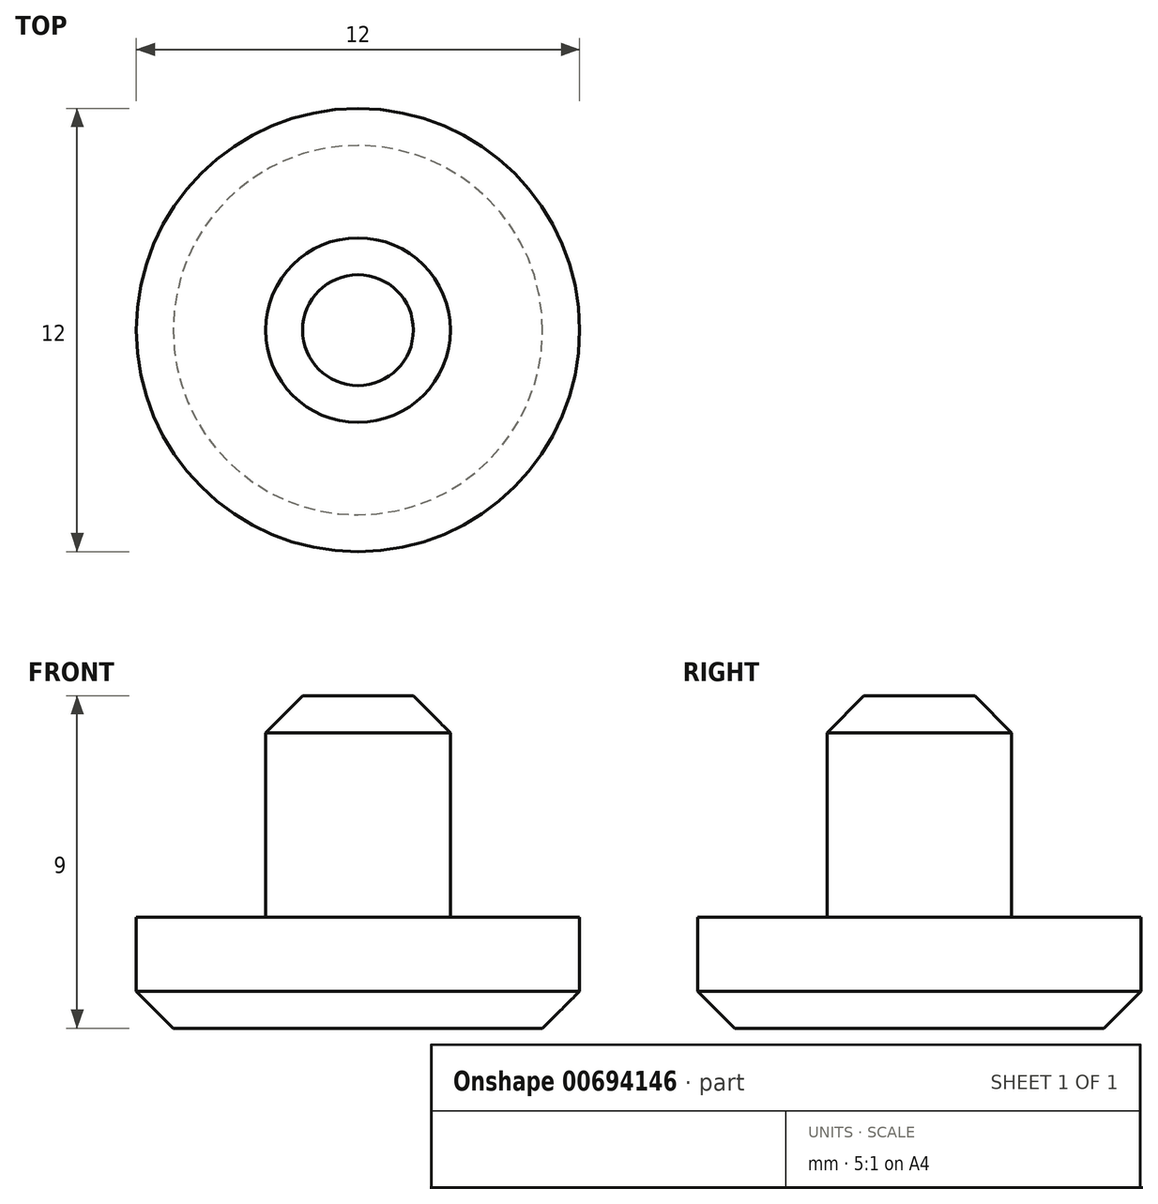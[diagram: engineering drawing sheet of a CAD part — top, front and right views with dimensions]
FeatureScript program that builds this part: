
annotation { "Feature Type Name" : "Feature", "Feature Type Description" : "" }
export const myFeature = defineFeature(function(context is Context, id is Id, definition is map)
    precondition{}
    {
        {
            var Q0;
            Q0=qCreatedBy(makeId("Top.planeOp"),FACE);
            var sketch = newSketch(context, id + "F0", { "sketchPlane" : qUnion([Q0])});
            skCircle(sketch, "E0", {"center": v(0, 0) * mm, "radius": 6 * mm});
            skCircle(sketch, "E1", {"center": v(0, 0) * mm, "radius": 2.5 * mm});
            skSolve(sketch);
        }
        {
            var Q0;
            Q0=makeQuery(id+"F0.imprint","IMPRINT",FACE,{"disambiguationData":[TD([[makeQuery(id+"F0.imprint","IMPRINT",EDGE,{"derivedFrom":sQuery(id+"F0.wireOp",EDGE,"E0")}),1.0]])]});
            var Q1;
            Q1=makeQuery(id+"F0.imprint","IMPRINT",FACE,{"disambiguationData":[TD([[makeQuery(id+"F0.imprint","IMPRINT",EDGE,{"derivedFrom":sQuery(id+"F0.wireOp",EDGE,"E1")}),1.0]])]});
            extrude(context, id + "F1", {"entities" : qUnion([Q0, Q1]), "oppositeDirection" : true, "depth" : 3 * mm, "offsetDistance" : 25 * mm});
        }
        {
            var Q0;
            Q0=makeQuery(id+"F0.imprint","IMPRINT",FACE,{"disambiguationData":[TD([[makeQuery(id+"F0.imprint","IMPRINT",EDGE,{"derivedFrom":sQuery(id+"F0.wireOp",EDGE,"E1")}),1.0]])]});
            extrude(context, id + "F2", {"entities" : qUnion([Q0]), "operationType" : NewBodyOperationType.ADD, "depth" : 6 * mm, "offsetDistance" : 25 * mm});
        }
        {
            var Q0;
            Q0=makeQuery(id+"F2.opExtrude","CAP_EDGE",EDGE,{"disambiguationData":[OSD([sQuery(id+"F0.wireOp",EDGE,"E1")])],"isStart":false});
            var Q1;
            Q1=makeQuery(id+"F1.opExtrude","CAP_EDGE",EDGE,{"disambiguationData":[OSD([sQuery(id+"F0.wireOp",EDGE,"E0")])],"isStart":false});
            chamfer(context, id + "F3", {"entities" : qUnion([Q0, Q1]), "width" : 1 * mm, "tangentPropagation" : true});
        }
    });
